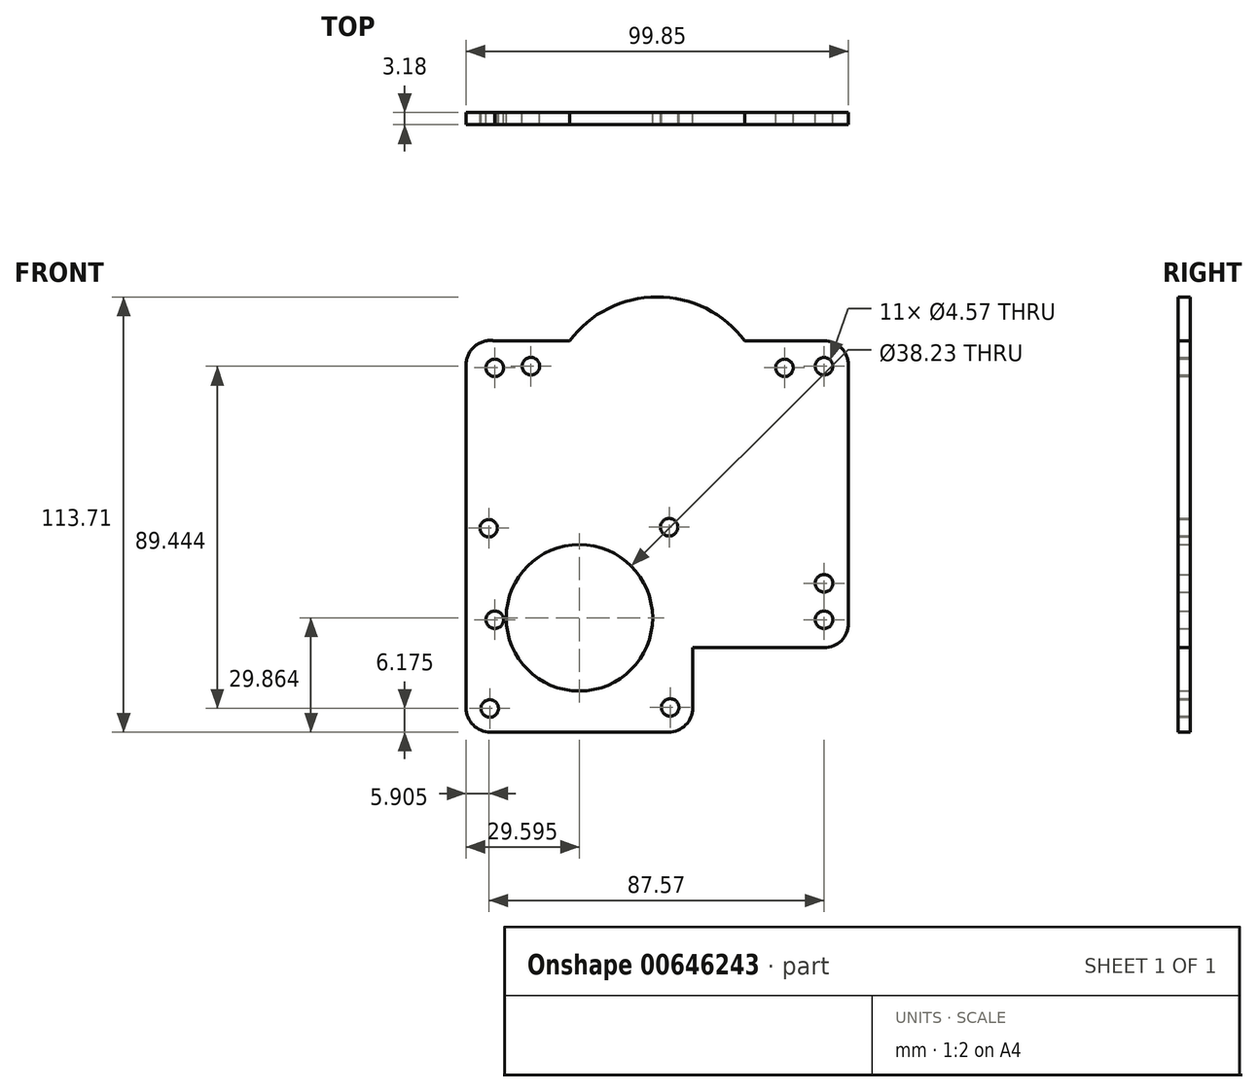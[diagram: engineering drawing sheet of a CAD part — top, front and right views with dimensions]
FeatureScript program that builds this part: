
annotation { "Feature Type Name" : "Feature", "Feature Type Description" : "" }
export const myFeature = defineFeature(function(context is Context, id is Id, definition is map)
    precondition{}
    {
        {
            var Q0;
            Q0=qCreatedBy(makeId("Front.planeOp"),FACE);
            var sketch = newSketch(context, id + "F0", { "sketchPlane" : qUnion([Q0])});
            skLineSegment(sketch, "E0", {"start": v(-34.76, 47.3) * mm, "end": v(-15.28, 47.3) * mm});
            skLineSegment(sketch, "E1", {"start": v(57.6, 40.94) * mm, "end": v(57.6, -26.52) * mm});
            skLineSegment(sketch, "E2", {"start": v(51.24, -32.87) * mm, "end": v(16.93, -32.87) * mm});
            skLineSegment(sketch, "E3", {"start": v(16.93, -32.87) * mm, "end": v(16.93, -48.59) * mm});
            skLineSegment(sketch, "E4", {"start": v(10.58, -54.94) * mm, "end": v(-35.9, -54.94) * mm});
            skLineSegment(sketch, "E5", {"start": v(-42.26, -48.59) * mm, "end": v(-42.26, 41.05) * mm});
            skArc(sketch, "E6", {"start": v(30.51, 47.3) * mm, "mid": v(7.62, 58.77) * mm, "end": v(-15.28, 47.3) * mm});
            skCircle(sketch, "E7", {"center": v(-12.67, -25.08) * mm, "radius": 19.11 * mm});
            skPoint(sketch, "E8.center", {"position": v(-42.26, 47.3) * mm});
            skPoint(sketch, "E9.2.0", {"position": v(-123.85, 54.02) * mm});
            skCircle(sketch, "E10", {"center": v(-36.35, -1.66) * mm, "radius": 2.29 * mm});
            skCircle(sketch, "E11.1.0", {"center": v(-36.08, -48.76) * mm, "radius": 2.29 * mm});
            skCircle(sketch, "E11.2.0", {"center": v(11.02, -48.5) * mm, "radius": 2.29 * mm});
            skCircle(sketch, "E11.3.0", {"center": v(10.75, -1.39) * mm, "radius": 2.29 * mm});
            skLineSegment(sketch, "E12.trimOffspring", {"start": v(30.51, 47.3) * mm, "end": v(51.24, 47.3) * mm});
            skCircle(sketch, "E13", {"center": v(51.22, -16.05) * mm, "radius": 2.29 * mm});
            skCircle(sketch, "E14", {"center": v(51.22, 40.68) * mm, "radius": 2.29 * mm});
            skCircle(sketch, "E15", {"center": v(-25.33, 40.68) * mm, "radius": 2.29 * mm});
            skPoint(sketch, "E16.visualSharp", {"position": v(57.6, 47.3) * mm});
            skArc(sketch, "E16.filletArc", {"start": v(57.6, 40.94) * mm, "mid": v(55.73, 45.43) * mm, "end": v(51.24, 47.3) * mm});
            skPoint(sketch, "E17.visualSharp", {"position": v(57.6, -32.87) * mm});
            skArc(sketch, "E17.filletArc", {"start": v(51.24, -32.87) * mm, "mid": v(55.73, -31.01) * mm, "end": v(57.6, -26.52) * mm});
            skPoint(sketch, "E18.visualSharp", {"position": v(16.93, -54.94) * mm});
            skArc(sketch, "E18.filletArc", {"start": v(10.58, -54.94) * mm, "mid": v(15.07, -53.08) * mm, "end": v(16.93, -48.59) * mm});
            skPoint(sketch, "E19.visualSharp", {"position": v(-42.26, -54.94) * mm});
            skArc(sketch, "E19.filletArc", {"start": v(-42.26, -48.59) * mm, "mid": v(-40.4, -53.08) * mm, "end": v(-35.9, -54.94) * mm});
            skArc(sketch, "E20.filletArc", {"start": v(-34.76, 47.3) * mm, "mid": v(-39.97, 45.92) * mm, "end": v(-42.26, 41.05) * mm});
            skCircle(sketch, "E21", {"center": v(40.88, 40.26) * mm, "radius": 2.29 * mm});
            skCircle(sketch, "E22", {"center": v(-34.76, 40.26) * mm, "radius": 2.29 * mm});
            skCircle(sketch, "E23", {"center": v(51.22, -25.58) * mm, "radius": 2.29 * mm});
            skCircle(sketch, "E24", {"center": v(-34.76, -25.58) * mm, "radius": 2.29 * mm});
            skSolve(sketch);
        }
        {
            var Q0;
            Q0 = qSketchRegion(id + "F0", true);
            extrude(context, id + "F1", {"entities" : qUnion([Q0]), "depth" : 3.17 * mm, "offsetDistance" : 25.4 * mm});
        }
    });
